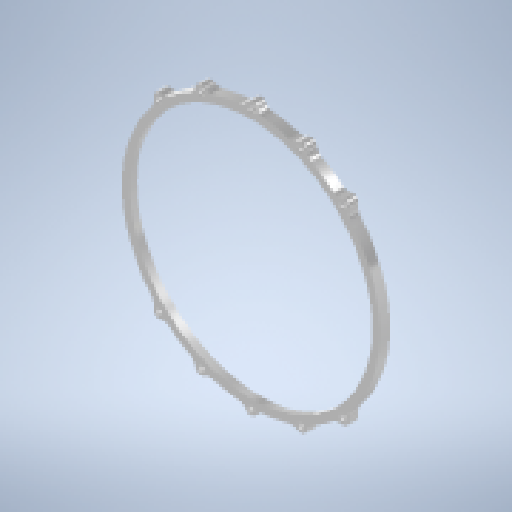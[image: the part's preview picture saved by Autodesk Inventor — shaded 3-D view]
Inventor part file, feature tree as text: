
AUTODESK INVENTOR PART (.ipt)
format: ipt  version: 2024 (Build 280153000, 153)  size: 287,744 bytes
history: native  units: mm
features: sketch x5, extrude x4, projected_geometry x3, other x1, fillet x1, pattern_circular x1, hole x1
ambient origin geometry x8: Origin, YZ Plane, XZ Plane, XY Plane, X Axis, Y Axis, Z Axis, Center Point
bodies: Body1 (feature_tree)
feature tree (16):
  other  "ソリッド1"
  extrude  "押し出し1"  Depth=122.0mm
  extrude  "押し出し2"  Depth=130.0mm
  extrude  "押し出し3"  Depth=3.0mm TaperAngle=0.0deg
  fillet  "フィレット1"  Radius=125.0mm
  pattern_circular  "円形状パターン1"  [2 undecoded]
  extrude  "押し出し4"  Depth=6.0mm
  hole  "穴1"  [1 undecoded]
  sketch  "スケッチ1"
  sketch  "スケッチ2"
  projected_geometry  "投影ループ1"
  sketch  "スケッチ3"
  projected_geometry  "投影ループ2"
  sketch  "スケッチ4"
  projected_geometry  "投影ループ3"
  sketch  "スケッチ5"
note: 3 required parameter values undecoded (feature->parameter linkage not recoverable at this tier; creation-order binding heuristic only, values carry confidence <= 0.55)
